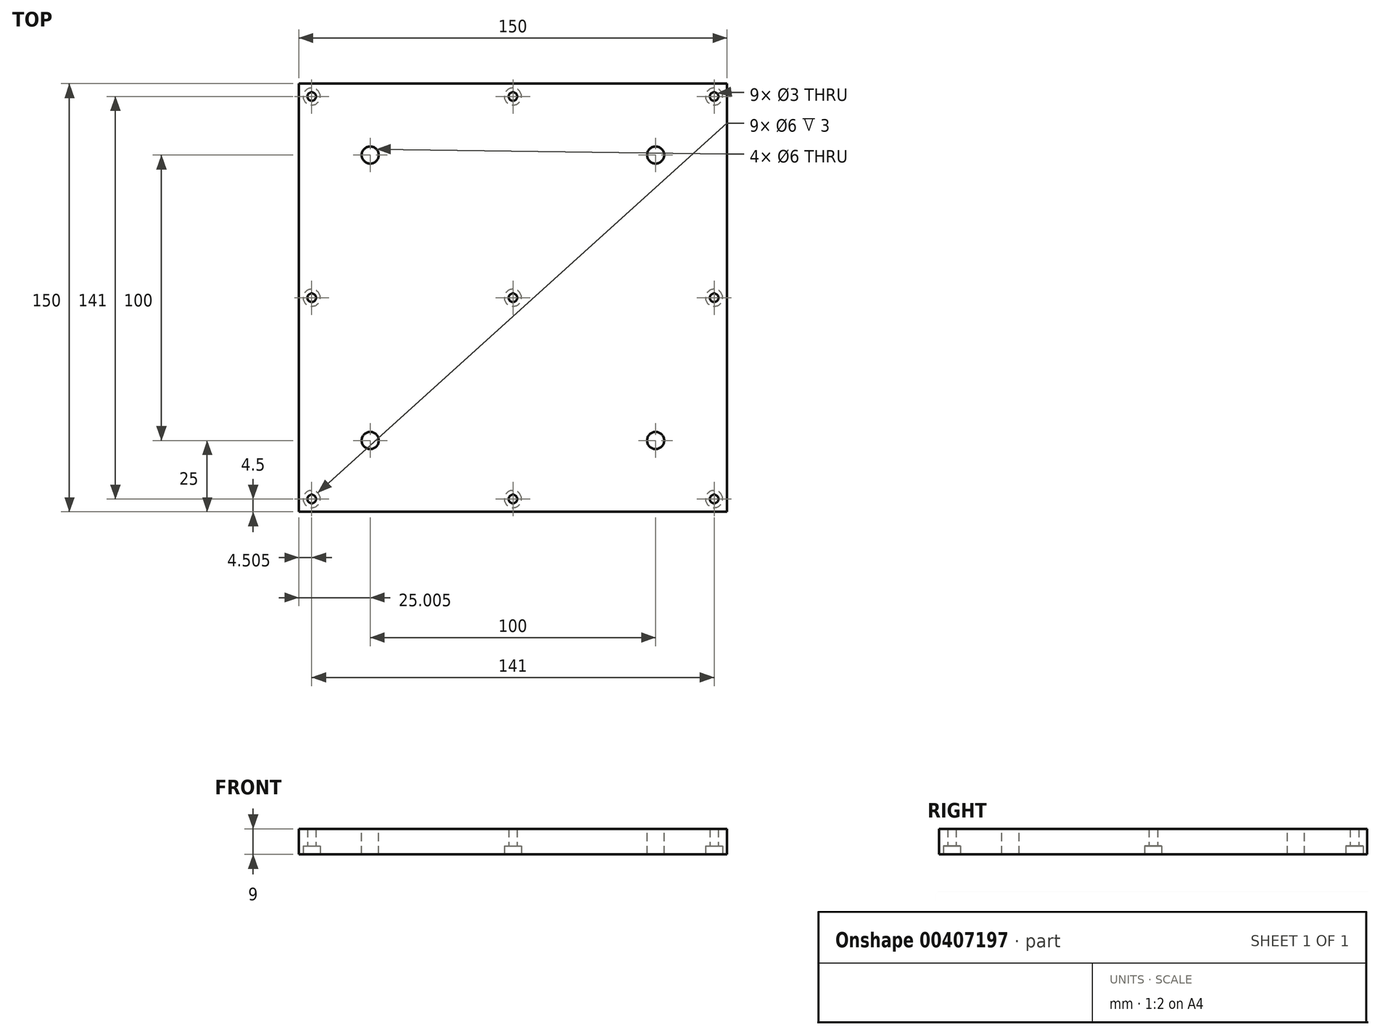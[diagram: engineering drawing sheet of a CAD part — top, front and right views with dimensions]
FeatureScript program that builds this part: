
annotation { "Feature Type Name" : "Feature", "Feature Type Description" : "" }
export const myFeature = defineFeature(function(context is Context, id is Id, definition is map)
    precondition{}
    {
        {
            var Q0;
            Q0=qCreatedBy(makeId("Top.planeOp"),FACE);
            var sketch = newSketch(context, id + "F0", { "sketchPlane" : qUnion([Q0])});
            skLineSegment(sketch, "E0.bottom", {"start": v(-149.07, -27.65) * mm, "end": v(0.93, -27.65) * mm});
            skLineSegment(sketch, "E0.top", {"start": v(-149.07, -177.65) * mm, "end": v(0.93, -177.65) * mm});
            skLineSegment(sketch, "E0.left", {"start": v(-149.07, -27.65) * mm, "end": v(-149.07, -177.65) * mm});
            skLineSegment(sketch, "E0.right", {"start": v(0.93, -27.65) * mm, "end": v(0.93, -177.65) * mm});
            skSolve(sketch);
        }
        {
            var Q0;
            Q0=qSketchRegion(id+"F0",true);
            extrude(context, id + "F1", {"entities" : qUnion([Q0]), "depth" : 9 * mm});
        }
        {
            var Q0;
            Q0=makeQuery(id+"F1.opExtrude","CAP_FACE",FACE,{"disambiguationData":[OSD([sQuery(id+"F0.wireOp",EDGE,"E0.bottom"),sQuery(id+"F0.wireOp",EDGE,"E0.top"),sQuery(id+"F0.wireOp",EDGE,"E0.left"),sQuery(id+"F0.wireOp",EDGE,"E0.right")])],"isStart":false});
            var sketch = newSketch(context, id + "F2", { "sketchPlane" : qUnion([Q0])});
            skLineSegment(sketch, "E1.bottom", {"start": v(-124.07, -52.65) * mm, "end": v(-24.07, -52.65) * mm, "construction": true});
            skLineSegment(sketch, "E1.top", {"start": v(-124.07, -152.65) * mm, "end": v(-24.07, -152.65) * mm, "construction": true});
            skLineSegment(sketch, "E1.left", {"start": v(-124.07, -52.65) * mm, "end": v(-124.07, -152.65) * mm, "construction": true});
            skLineSegment(sketch, "E1.right", {"start": v(-24.07, -52.65) * mm, "end": v(-24.07, -152.65) * mm, "construction": true});
            skCircle(sketch, "E2", {"center": v(-124.07, -52.65) * mm, "radius": 3 * mm});
            skCircle(sketch, "E3", {"center": v(-124.07, -152.65) * mm, "radius": 3 * mm});
            skCircle(sketch, "E4", {"center": v(-24.07, -152.65) * mm, "radius": 3 * mm});
            skCircle(sketch, "E5", {"center": v(-24.07, -52.65) * mm, "radius": 3 * mm});
            skSolve(sketch);
        }
        {
            var Q0;
            Q0=qSketchRegion(id+"F2",true);
            extrude(context, id + "F3", {"entities" : qUnion([Q0]), "operationType" : NewBodyOperationType.REMOVE, "endBound" : BoundingType.THROUGH_ALL, "oppositeDirection" : true, "depth" : 25 * mm});
        }
        {
            var Q0;
            Q0=makeQuery(id+"F1.opExtrude","CAP_FACE",FACE,{"disambiguationData":[OSD([sQuery(id+"F0.wireOp",EDGE,"E0.bottom"),sQuery(id+"F0.wireOp",EDGE,"E0.top"),sQuery(id+"F0.wireOp",EDGE,"E0.left"),sQuery(id+"F0.wireOp",EDGE,"E0.right")])],"isStart":true});
            var sketch = newSketch(context, id + "F4", { "sketchPlane" : qUnion([Q0])});
            skLineSegment(sketch, "E6.bottom", {"start": v(-144.57, 173.15) * mm, "end": v(-3.57, 173.15) * mm, "construction": true});
            skLineSegment(sketch, "E6.top", {"start": v(-144.57, 32.15) * mm, "end": v(-3.57, 32.15) * mm, "construction": true});
            skLineSegment(sketch, "E6.left", {"start": v(-144.57, 173.15) * mm, "end": v(-144.57, 32.15) * mm, "construction": true});
            skLineSegment(sketch, "E6.right", {"start": v(-3.57, 173.15) * mm, "end": v(-3.57, 32.15) * mm, "construction": true});
            skCircle(sketch, "E7", {"center": v(-144.57, 173.15) * mm, "radius": 1.5 * mm});
            skCircle(sketch, "E8", {"center": v(-74.07, 173.15) * mm, "radius": 1.5 * mm});
            skCircle(sketch, "E9", {"center": v(-3.57, 173.15) * mm, "radius": 1.5 * mm});
            skCircle(sketch, "E10", {"center": v(-3.57, 102.65) * mm, "radius": 1.5 * mm});
            skCircle(sketch, "E11", {"center": v(-3.57, 32.15) * mm, "radius": 1.5 * mm});
            skCircle(sketch, "E12", {"center": v(-74.07, 32.15) * mm, "radius": 1.5 * mm});
            skCircle(sketch, "E13", {"center": v(-144.57, 32.15) * mm, "radius": 1.5 * mm});
            skCircle(sketch, "E14", {"center": v(-144.57, 102.65) * mm, "radius": 1.5 * mm});
            skLineSegment(sketch, "E15", {"start": v(-74.07, 173.15) * mm, "end": v(-74.07, 32.15) * mm, "construction": true});
            skLineSegment(sketch, "E16", {"start": v(-144.57, 102.65) * mm, "end": v(-3.57, 102.65) * mm, "construction": true});
            skCircle(sketch, "E17", {"center": v(-74.07, 102.65) * mm, "radius": 1.5 * mm});
            skSolve(sketch);
        }
        {
            var Q0;
            Q0 = qSketchRegion(id + "F4", true);
            extrude(context, id + "F5", {"entities" : qUnion([Q0]), "operationType" : NewBodyOperationType.REMOVE, "endBound" : BoundingType.THROUGH_ALL, "oppositeDirection" : true, "depth" : 25 * mm});
        }
        {
            var Q0;
            Q0=makeQuery(id+"F1.opExtrude","CAP_FACE",FACE,{"disambiguationData":[OSD([sQuery(id+"F0.wireOp",EDGE,"E0.bottom"),sQuery(id+"F0.wireOp",EDGE,"E0.top"),sQuery(id+"F0.wireOp",EDGE,"E0.left"),sQuery(id+"F0.wireOp",EDGE,"E0.right")])],"isStart":true});
            var sketch = newSketch(context, id + "F6", { "sketchPlane" : qUnion([Q0])});
            skCircle(sketch, "E18", {"center": v(-144.57, 173.15) * mm, "radius": 3 * mm});
            skCircle(sketch, "E19", {"center": v(-74.07, 173.15) * mm, "radius": 3 * mm});
            skCircle(sketch, "E20", {"center": v(-3.57, 173.15) * mm, "radius": 3 * mm});
            skCircle(sketch, "E21", {"center": v(-3.57, 102.65) * mm, "radius": 3 * mm});
            skCircle(sketch, "E22", {"center": v(-3.57, 32.15) * mm, "radius": 3 * mm});
            skCircle(sketch, "E23", {"center": v(-74.07, 32.15) * mm, "radius": 3 * mm});
            skCircle(sketch, "E24", {"center": v(-144.57, 32.15) * mm, "radius": 3 * mm});
            skCircle(sketch, "E25", {"center": v(-144.57, 102.65) * mm, "radius": 3 * mm});
            skCircle(sketch, "E26", {"center": v(-74.07, 102.65) * mm, "radius": 3 * mm});
            skSolve(sketch);
        }
        {
            var Q0;
            Q0=makeQuery(id+"F6.imprint","IMPRINT",FACE,{"disambiguationData":[TD([[makeQuery(id+"F6.imprint","IMPRINT",EDGE,{"derivedFrom":sQuery(id+"F6.wireOp",EDGE,"E18")}),1.0]])]});
            var Q1;
            Q1=makeQuery(id+"F6.imprint","IMPRINT",FACE,{"disambiguationData":[TD([[makeQuery(id+"F6.imprint","IMPRINT",EDGE,{"derivedFrom":sQuery(id+"F6.wireOp",EDGE,"E19")}),1.0]])]});
            var Q2;
            Q2=makeQuery(id+"F6.imprint","IMPRINT",FACE,{"disambiguationData":[TD([[makeQuery(id+"F6.imprint","IMPRINT",EDGE,{"derivedFrom":sQuery(id+"F6.wireOp",EDGE,"E20")}),1.0]])]});
            var Q3;
            Q3=makeQuery(id+"F6.imprint","IMPRINT",FACE,{"disambiguationData":[TD([[makeQuery(id+"F6.imprint","IMPRINT",EDGE,{"derivedFrom":sQuery(id+"F6.wireOp",EDGE,"E21")}),1.0]])]});
            var Q4;
            Q4=makeQuery(id+"F6.imprint","IMPRINT",FACE,{"disambiguationData":[TD([[makeQuery(id+"F6.imprint","IMPRINT",EDGE,{"derivedFrom":sQuery(id+"F6.wireOp",EDGE,"E26")}),1.0]])]});
            var Q5;
            Q5=makeQuery(id+"F6.imprint","IMPRINT",FACE,{"disambiguationData":[TD([[makeQuery(id+"F6.imprint","IMPRINT",EDGE,{"derivedFrom":sQuery(id+"F6.wireOp",EDGE,"E25")}),1.0]])]});
            var Q6;
            Q6=makeQuery(id+"F6.imprint","IMPRINT",FACE,{"disambiguationData":[TD([[makeQuery(id+"F6.imprint","IMPRINT",EDGE,{"derivedFrom":sQuery(id+"F6.wireOp",EDGE,"E24")}),1.0]])]});
            var Q7;
            Q7=makeQuery(id+"F6.imprint","IMPRINT",FACE,{"disambiguationData":[TD([[makeQuery(id+"F6.imprint","IMPRINT",EDGE,{"derivedFrom":sQuery(id+"F6.wireOp",EDGE,"E23")}),1.0]])]});
            var Q8;
            Q8=makeQuery(id+"F6.imprint","IMPRINT",FACE,{"disambiguationData":[TD([[makeQuery(id+"F6.imprint","IMPRINT",EDGE,{"derivedFrom":sQuery(id+"F6.wireOp",EDGE,"E22")}),1.0]])]});
            extrude(context, id + "F7", {"entities" : qUnion([Q0, Q1, Q2, Q3, Q4, Q5, Q6, Q7, Q8]), "operationType" : NewBodyOperationType.REMOVE, "oppositeDirection" : true, "depth" : 3 * mm});
        }
    });
